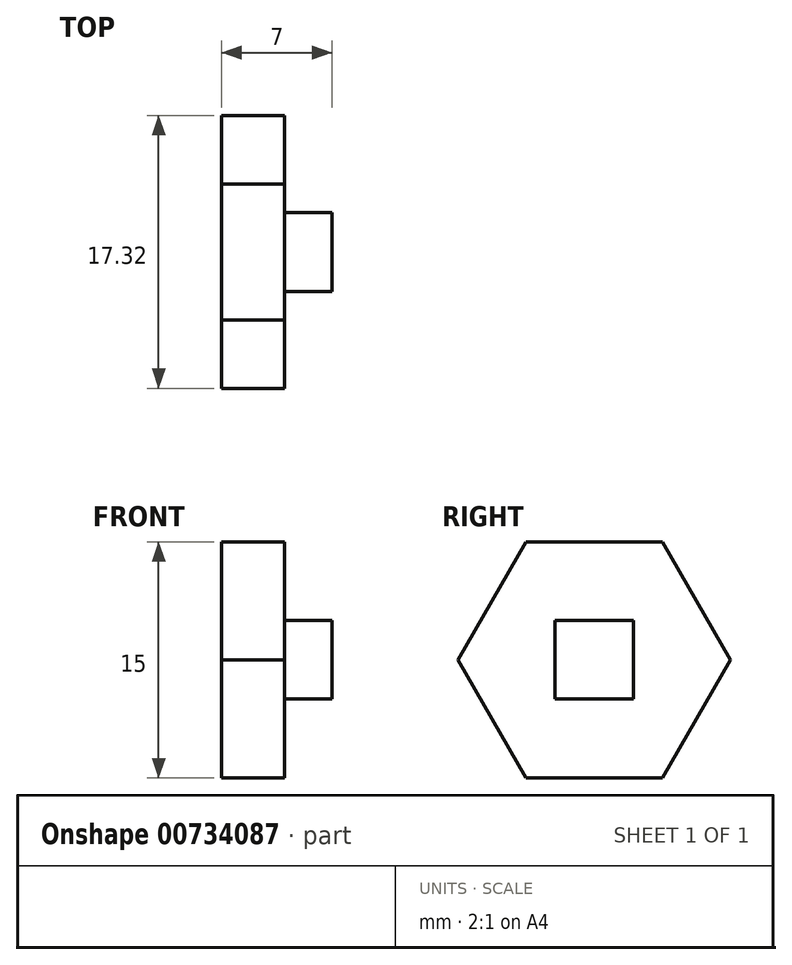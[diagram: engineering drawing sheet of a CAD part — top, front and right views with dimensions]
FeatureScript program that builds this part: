
annotation { "Feature Type Name" : "Feature", "Feature Type Description" : "" }
export const myFeature = defineFeature(function(context is Context, id is Id, definition is map)
    precondition{}
    {
        {
            var Q0;
            Q0=qCreatedBy(makeId("Right.planeOp"),FACE);
            var sketch = newSketch(context, id + "F0", { "sketchPlane" : qUnion([Q0])});
            skLineSegment(sketch, "E0.bottom", {"start": v(44.1, 36.3) * mm, "end": v(39.1, 36.3) * mm});
            skLineSegment(sketch, "E0.top", {"start": v(44.1, 31.3) * mm, "end": v(39.1, 31.3) * mm});
            skLineSegment(sketch, "E0.left", {"start": v(44.1, 36.3) * mm, "end": v(44.1, 31.3) * mm});
            skLineSegment(sketch, "E0.right", {"start": v(39.1, 36.3) * mm, "end": v(39.1, 31.3) * mm});
            skCircle(sketch, "E1.cCircle", {"center": v(41.6, 33.8) * mm, "radius": 7.5 * mm, "construction": true});
            skPoint(sketch, "E1.cCircle.centerSnap0", {"position": v(39.1, 33.8) * mm});
            skPoint(sketch, "E1.cCircle.centerSnap1", {"position": v(41.6, 36.3) * mm});
            skLineSegment(sketch, "E1.0", {"start": v(37.28, 41.3) * mm, "end": v(45.94, 41.3) * mm});
            skLineSegment(sketch, "E1.1", {"start": v(45.94, 41.3) * mm, "end": v(50.27, 33.8) * mm});
            skLineSegment(sketch, "E1.2", {"start": v(50.27, 33.8) * mm, "end": v(45.94, 26.3) * mm});
            skLineSegment(sketch, "E1.3", {"start": v(45.94, 26.3) * mm, "end": v(37.28, 26.3) * mm});
            skLineSegment(sketch, "E1.4", {"start": v(37.28, 26.3) * mm, "end": v(32.95, 33.8) * mm});
            skLineSegment(sketch, "E1.5", {"start": v(32.95, 33.8) * mm, "end": v(37.28, 41.3) * mm});
            skPoint(sketch, "E1.0.midPoint", {"position": v(41.6, 41.3) * mm});
            skSolve(sketch);
        }
        {
            var Q0;
            Q0=makeQuery(id+"F0.imprint","IMPRINT",FACE,{"disambiguationData":[TD([[makeQuery(id+"F0.imprint","IMPRINT",EDGE,{"derivedFrom":sQuery(id+"F0.wireOp",EDGE,"E0.bottom")}),1.0]])]});
            extrude(context, id + "F1", {"entities" : qUnion([Q0]), "depth" : 3 * mm, "offsetDistance" : 25 * mm});
        }
        {
            var Q0;
            Q0=makeQuery(id+"F0.imprint","IMPRINT",FACE,{"disambiguationData":[TD([[makeQuery(id+"F0.imprint","IMPRINT",EDGE,{"derivedFrom":sQuery(id+"F0.wireOp",EDGE,"E0.bottom")}),-1.0]])]});
            var Q1;
            Q1=makeQuery(id+"F0.imprint","IMPRINT",FACE,{"disambiguationData":[TD([[makeQuery(id+"F0.imprint","IMPRINT",EDGE,{"derivedFrom":sQuery(id+"F0.wireOp",EDGE,"E0.bottom")}),1.0]])]});
            extrude(context, id + "F2", {"entities" : qUnion([Q0, Q1]), "operationType" : NewBodyOperationType.ADD, "depth" : -4 * mm, "offsetDistance" : 25 * mm});
        }
    });
